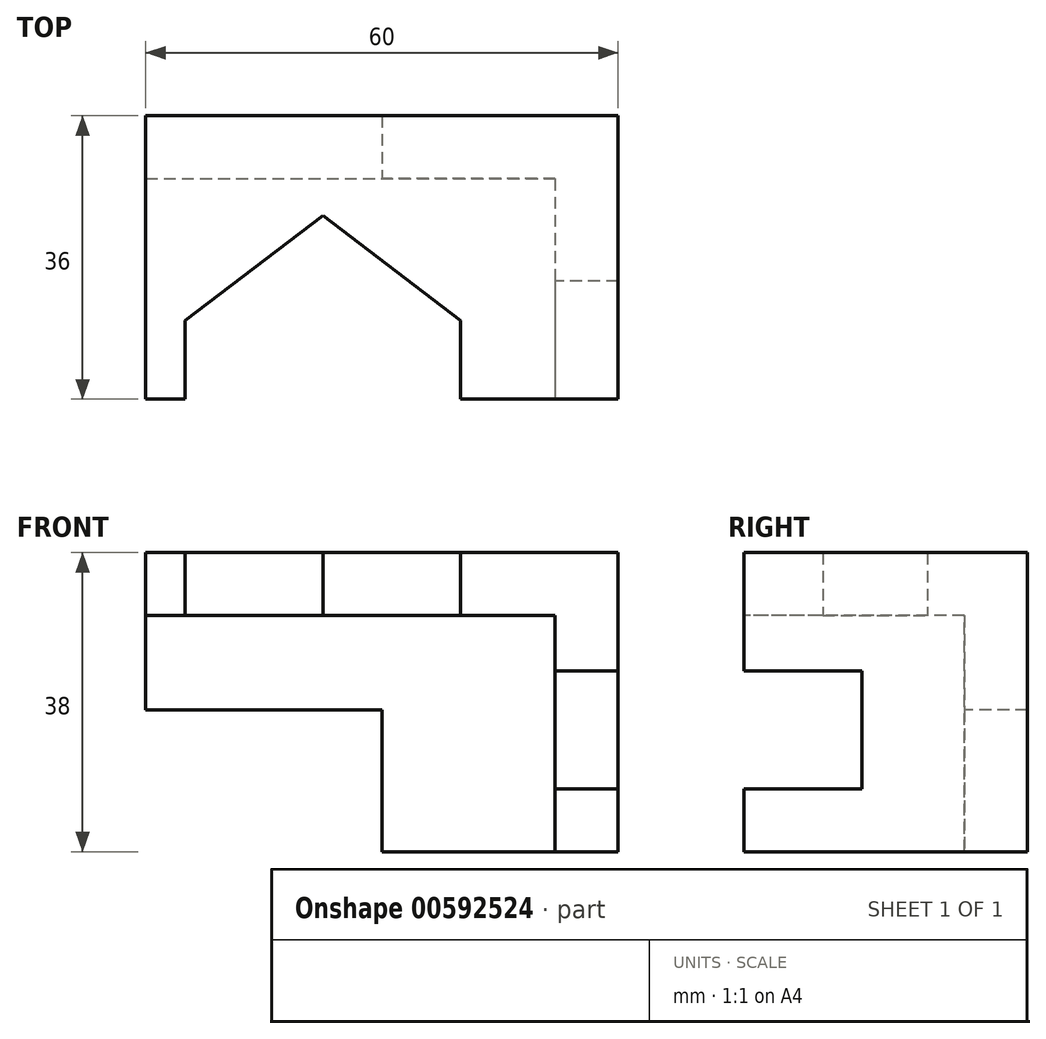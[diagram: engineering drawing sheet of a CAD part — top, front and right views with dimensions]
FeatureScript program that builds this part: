
annotation { "Feature Type Name" : "Feature", "Feature Type Description" : "" }
export const myFeature = defineFeature(function(context is Context, id is Id, definition is map)
    precondition{}
    {
        {
            var Q0;
            Q0=qCreatedBy(makeId("Front.planeOp"),FACE);
            var sketch = newSketch(context, id + "F0", { "sketchPlane" : qUnion([Q0])});
            skLineSegment(sketch, "E0.bottom", {"start": v(30, 19) * mm, "end": v(-30, 19) * mm});
            skLineSegment(sketch, "E0.top", {"start": v(30, -19) * mm, "end": v(-30, -19) * mm});
            skLineSegment(sketch, "E0.left", {"start": v(30, 19) * mm, "end": v(30, -19) * mm});
            skLineSegment(sketch, "E0.right", {"start": v(-30, 19) * mm, "end": v(-30, -19) * mm});
            skPoint(sketch, "E0.middle", {"position": v(0, 0) * mm});
            skSolve(sketch);
        }
        {
            var Q0;
            Q0 = qSketchRegion(id + "F0", true);
            extrude(context, id + "F1", {"entities" : qUnion([Q0]), "depth" : 36 * mm, "offsetDistance" : 25 * mm});
        }
        {
            var Q0;
            Q0=makeQuery(id+"F1.opExtrude","CAP_FACE",FACE,{"disambiguationData":[OSD([sQuery(id+"F0.wireOp",EDGE,"E0.bottom"),sQuery(id+"F0.wireOp",EDGE,"E0.top"),sQuery(id+"F0.wireOp",EDGE,"E0.left"),sQuery(id+"F0.wireOp",EDGE,"E0.right")])],"isStart":false});
            var sketch = newSketch(context, id + "F2", { "sketchPlane" : qUnion([Q0])});
            skLineSegment(sketch, "E1.bottom", {"start": v(30, -19) * mm, "end": v(22, -19) * mm});
            skLineSegment(sketch, "E1.top", {"start": v(30, -11) * mm, "end": v(22, -11) * mm});
            skLineSegment(sketch, "E1.left", {"start": v(30, -19) * mm, "end": v(30, -11) * mm});
            skLineSegment(sketch, "E1.right", {"start": v(22, -19) * mm, "end": v(22, -11) * mm});
            skLineSegment(sketch, "E2", {"start": v(30, 4) * mm, "end": v(30, 19) * mm});
            skLineSegment(sketch, "E3", {"start": v(30, 19) * mm, "end": v(10, 19) * mm});
            skLineSegment(sketch, "E4", {"start": v(10, 19) * mm, "end": v(10, 11) * mm});
            skLineSegment(sketch, "E5", {"start": v(10, 11) * mm, "end": v(22, 11) * mm});
            skLineSegment(sketch, "E6", {"start": v(22, 11) * mm, "end": v(22, 4) * mm});
            skLineSegment(sketch, "E7", {"start": v(22, 4) * mm, "end": v(30, 4) * mm});
            skLineSegment(sketch, "E8", {"start": v(22, 4) * mm, "end": v(22, -11) * mm});
            skLineSegment(sketch, "E9", {"start": v(30, 4) * mm, "end": v(30, -11) * mm});
            skLineSegment(sketch, "E10", {"start": v(-30, -1) * mm, "end": v(0, -1) * mm});
            skLineSegment(sketch, "E11", {"start": v(0, -1) * mm, "end": v(0, -19) * mm});
            skLineSegment(sketch, "E12", {"start": v(0, -19) * mm, "end": v(-30, -19) * mm});
            skLineSegment(sketch, "E13", {"start": v(-30, -19) * mm, "end": v(-30, -1) * mm});
            skLineSegment(sketch, "E14", {"start": v(-30, 19) * mm, "end": v(-30, 11) * mm});
            skLineSegment(sketch, "E15", {"start": v(-30, 11) * mm, "end": v(-25, 11) * mm});
            skLineSegment(sketch, "E16", {"start": v(-25, 11) * mm, "end": v(-25, 19) * mm});
            skLineSegment(sketch, "E17", {"start": v(-25, 19) * mm, "end": v(-30, 19) * mm});
            skLineSegment(sketch, "E18", {"start": v(-25, 11) * mm, "end": v(10, 11) * mm});
            skLineSegment(sketch, "E19", {"start": v(-25, 19) * mm, "end": v(10, 19) * mm});
            skSolve(sketch);
        }
        {
            var Q0;
            Q0=makeQuery(id+"F2.imprint","IMPRINT",FACE,{"disambiguationData":[TD([[makeQuery(id+"F2.imprint","IMPRINT",EDGE,{"derivedFrom":sQuery(id+"F2.wireOp",EDGE,"E1.top")}),-1.0]])]});
            extrude(context, id + "F3", {"entities" : qUnion([Q0]), "operationType" : NewBodyOperationType.REMOVE, "oppositeDirection" : true, "depth" : 15 * mm, "offsetDistance" : 25 * mm});
        }
        {
            var Q0;
            {var subQ5=sQuery(id+"F2.wireOp",EDGE,"E1.right");Q0=makeQuery(id+"F2.imprint","IMPRINT",FACE,{"disambiguationData":[TD([[makeQuery(id+"F2.imprint","IMPRINT",EDGE,{"derivedFrom":subQ5}),1.0]])]});}
            extrude(context, id + "F4", {"entities" : qUnion([Q0]), "operationType" : NewBodyOperationType.REMOVE, "oppositeDirection" : true, "depth" : 28 * mm, "offsetDistance" : 25 * mm});
        }
        {
            var Q0;
            Q0=makeQuery(id+"F2.imprint","IMPRINT",FACE,{"disambiguationData":[TD([[makeQuery(id+"F2.imprint","IMPRINT",EDGE,{"derivedFrom":sQuery(id+"F2.wireOp",EDGE,"E10")}),-1.0]])]});
            extrude(context, id + "F5", {"entities" : qUnion([Q0]), "operationType" : NewBodyOperationType.REMOVE, "endBound" : BoundingType.THROUGH_ALL, "oppositeDirection" : true, "depth" : 25 * mm, "offsetDistance" : 25 * mm});
        }
        {
            var Q0;
            Q0=makeQuery(id+"F2.imprint","IMPRINT",FACE,{"disambiguationData":[TD([[makeQuery(id+"F2.imprint","IMPRINT",EDGE,{"derivedFrom":sQuery(id+"F2.wireOp",EDGE,"E4")}),-1.0]])]});
            extrude(context, id + "F6", {"entities" : qUnion([Q0]), "operationType" : NewBodyOperationType.REMOVE, "oppositeDirection" : true, "depth" : 10 * mm, "offsetDistance" : 25 * mm});
        }
        {
            var Q0;
            Q0=makeQuery(id+"F4.boolean.opBoolean","COPY",FACE,{"derivedFrom":makeQuery(id+"F4.opExtrude","SWEPT_FACE",FACE,{"disambiguationData":[OSD([sQuery(id+"F2.wireOp",EDGE,"E5"),sQuery(id+"F2.wireOp",EDGE,"E15"),sQuery(id+"F2.wireOp",EDGE,"E18")])]})});
            var sketch = newSketch(context, id + "F7", { "sketchPlane" : qUnion([Q0])});
            skLineSegment(sketch, "E20", {"start": v(-7.5, 32.67) * mm, "end": v(-7.5, 12.67) * mm, "construction": true});
            skPoint(sketch, "E20.startSnap0", {"position": v(-7.5, 26) * mm});
            skLineSegment(sketch, "E21", {"start": v(-7.5, 12.67) * mm, "end": v(-30, 12.67) * mm, "construction": true});
            skLineSegment(sketch, "E22", {"start": v(-7.5, 12.67) * mm, "end": v(10, 26) * mm});
            skLineSegment(sketch, "E23", {"start": v(10, 26) * mm, "end": v(-25, 26) * mm});
            skLineSegment(sketch, "E24", {"start": v(-25, 26) * mm, "end": v(-7.5, 12.67) * mm});
            skSolve(sketch);
        }
        {
            var Q0;
            Q0 = qSketchRegion(id + "F7", true);
            extrude(context, id + "F8", {"entities" : qUnion([Q0]), "operationType" : NewBodyOperationType.REMOVE, "endBound" : BoundingType.THROUGH_ALL, "oppositeDirection" : true, "depth" : 25 * mm, "offsetDistance" : 25 * mm});
        }
    });
